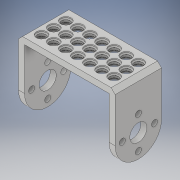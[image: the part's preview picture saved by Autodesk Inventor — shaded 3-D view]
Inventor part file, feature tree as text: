
AUTODESK INVENTOR PART (.ipt)
format: ipt  version: 2017 (Build 210142000, 142)  size: 368,640 bytes
history: native  units: in
note: dims shown in document units (in); Inventor stores cm internally (conversion verified against a paired STEP export)
features: extrude x5, sketch x5, chamfer x3, pattern_linear x2, plane x1, mirror x1
ambient origin geometry x8: Origin, YZ Plane, XZ Plane, XY Plane, X Axis, Y Axis, Z Axis, Center Point
bodies: Solid1 (feature_tree)
feature tree (17):
  extrude  "Extrusion1"  Depth=0.9055in
  extrude  "Extrusion2"  Depth=0.9055in
  plane  "Work Plane1"
  mirror  "Mirror1"
  extrude  "Extrusion3"  Depth=0.315in
  extrude  "Extrusion4"  Depth=0.1181in TaperAngle=0.0deg
  extrude  "Extrusion5"  Depth=0.0787in TaperAngle=0.0deg
  chamfer  "Chamfer1"  Distance=0.1614in
  chamfer  "Chamfer2"  Distance=0.8268in
  pattern_linear  "Rectangular Pattern1"  Spacing1=0.2047in  [1 undecoded]
  pattern_linear  "Rectangular Pattern2"  Spacing1=0.0394in  [1 undecoded]
  chamfer  "Chamfer3"  Distance=0.2047in
  sketch  "Sketch2"  dims[d0=0.9055in d2=0.9449in]
  sketch  "Sketch3"  dims[d3=0.9055in d4=0.3346in]
  sketch  "Sketch4"  dims[d5=0.1181in d6=0.315in]
  sketch  "Sketch5"  dims[d7=1.5748in d9=360.0deg d11=0.1181in d12=0.0in]
  sketch  "Sketch7"  dims[d13=0.1181in d14=0.8268in d15=0.0in d16=0.1614in d17=0.8268in d18=0.0in d19=0.2047in d20=0.0394in d21=0.0in d22=0.2047in d23=0.0394in d24=0.0in d25=0.0197in d26=0.0787in d27=45.0deg d28=0.0197in d29=0.0787in d30=45.0deg d31=0.7874in d33=0.2362in d34=0.7874in d36=0.2362in d37=1.5748in d39=0.2362in d40=1.5748in d42=0.2362in d43=0.0787in d44=0.0787in d45=45.0deg]
note: 2 required parameter values undecoded (feature->parameter linkage not recoverable at this tier; creation-order binding heuristic only, values carry confidence <= 0.55)
